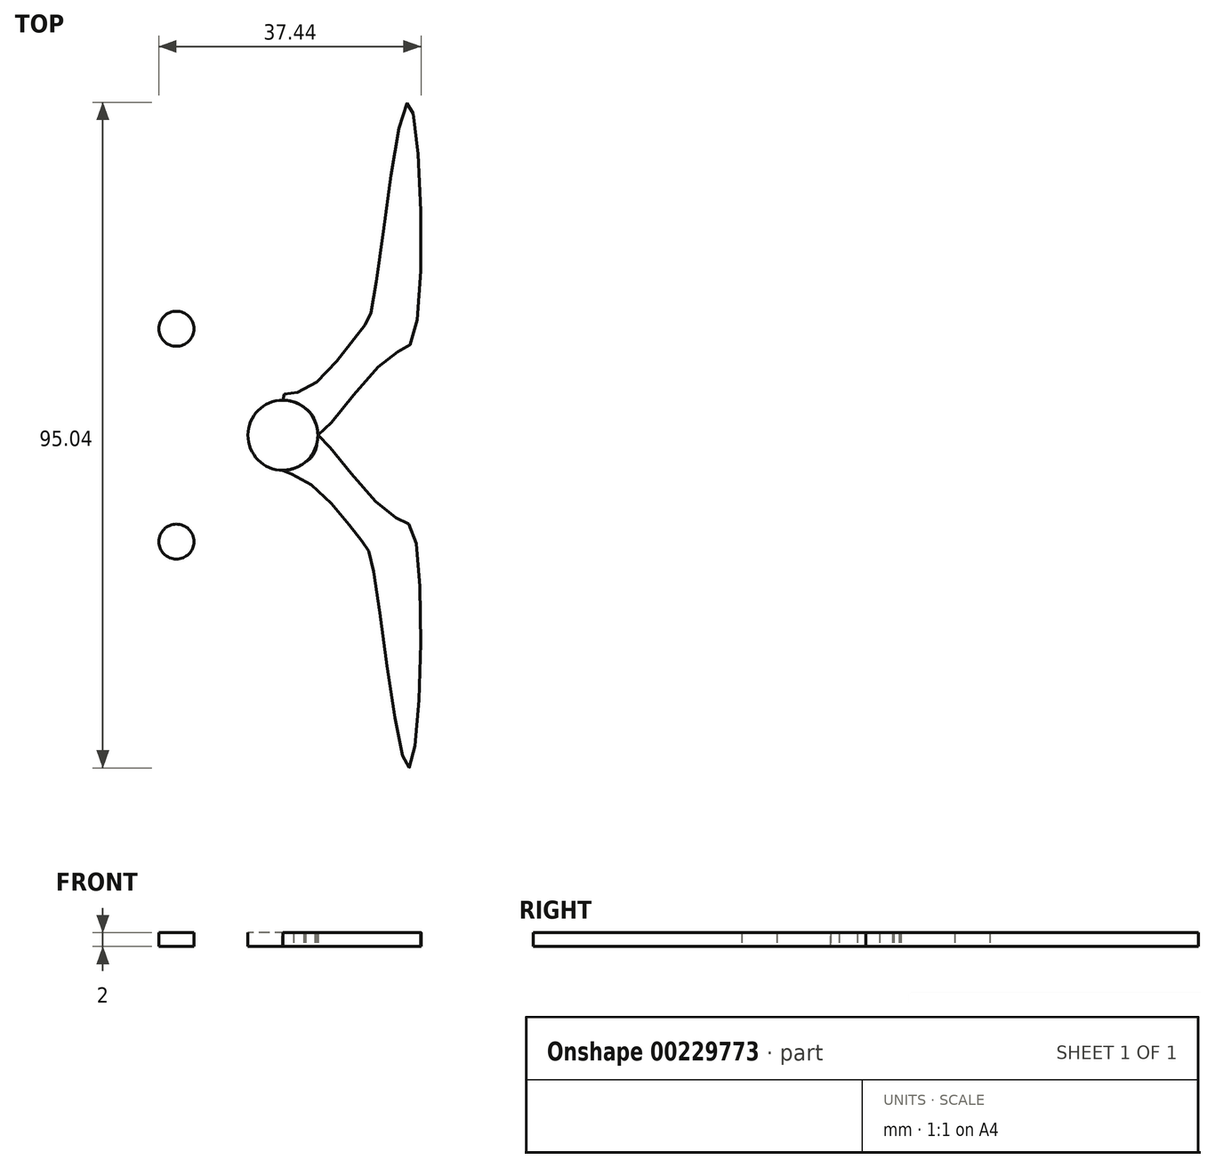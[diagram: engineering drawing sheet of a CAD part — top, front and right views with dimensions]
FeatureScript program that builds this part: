
annotation { "Feature Type Name" : "Feature", "Feature Type Description" : "" }
export const myFeature = defineFeature(function(context is Context, id is Id, definition is map)
    precondition{}
    {
        {
            var Q0;
            Q0=qCreatedBy(makeId("Top.planeOp"),FACE);
            var sketch = newSketch(context, id + "F0", { "sketchPlane" : qUnion([Q0])});
            skCircle(sketch, "E0", {"center": v(0, 0) * mm, "radius": 5 * mm});
            skCircle(sketch, "E1", {"center": v(-15.2, 15.2) * mm, "radius": 2.5 * mm});
            skFitSpline(sketch, "E2", {"points": [v(-5, 0) * mm, v(-15.31, 11.3) * mm, v(-18.74, 14.12) * mm, v(-17.97, 47.52) * mm, v(-12.83, 18.58) * mm, v(-11.2, 15.06) * mm, v(-3.24, 6.5) * mm, v(0, 5.73) * mm, v(0, 5) * mm, v(-5, 0) * mm, v(-5, 0) * mm, v(-5, 0) * mm]});
            skFitSpline(sketch, "E3.MirrorC", {"points": [v(5, 0) * mm, v(15.31, 11.3) * mm, v(18.74, 14.12) * mm, v(17.97, 47.52) * mm, v(12.83, 18.58) * mm, v(11.2, 15.06) * mm, v(3.24, 6.5) * mm, v(0, 5.73) * mm, v(0, 5) * mm, v(5, 0) * mm, v(5, 0) * mm, v(5, 0) * mm]});
            skCircle(sketch, "E4.MirrorC", {"center": v(15.2, 15.2) * mm, "radius": 2.5 * mm});
            skCircle(sketch, "E5.MirrorC", {"center": v(-15.2, -15.2) * mm, "radius": 2.5 * mm});
            skCircle(sketch, "E6.MirrorC", {"center": v(15.2, -15.2) * mm, "radius": 2.5 * mm});
            skFitSpline(sketch, "E7", {"points": [v(0, 5.73) * mm, v(-3.24, 6.5) * mm, v(-11.2, 15.06) * mm, v(-11.2, 16.1) * mm, v(-12.83, 18.58) * mm, v(-17.97, 47.52) * mm, v(-18.74, 14.12) * mm, v(-15.31, 11.3) * mm, v(-5, 0) * mm, v(0, 5) * mm, v(0, 5) * mm, v(0, 5) * mm, v(0, 5) * mm, v(0, 5.73) * mm]});
            skFitSpline(sketch, "E8", {"points": [v(0, 5) * mm, v(0, 5.73) * mm, v(3.24, 6.5) * mm, v(11.2, 15.06) * mm, v(12.83, 18.58) * mm, v(17.97, 47.52) * mm, v(18.74, 14.12) * mm, v(15.31, 11.3) * mm, v(5, 0) * mm, v(0, 5) * mm, v(0, 5) * mm, v(0, 5) * mm]});
            skFitSpline(sketch, "E9.MirrorC", {"points": [v(0, -5) * mm, v(0, -5.73) * mm, v(3.24, -6.5) * mm, v(11.2, -15.06) * mm, v(12.83, -18.58) * mm, v(17.97, -47.52) * mm, v(18.74, -14.12) * mm, v(15.31, -11.3) * mm, v(5, 0) * mm, v(0, -5) * mm, v(0, -5) * mm, v(0, -5) * mm]});
            skFitSpline(sketch, "E10.MirrorC", {"points": [v(0, -5.73) * mm, v(-3.24, -6.5) * mm, v(-11.2, -15.06) * mm, v(-11.2, -16.1) * mm, v(-12.83, -18.58) * mm, v(-17.97, -47.52) * mm, v(-18.74, -14.12) * mm, v(-15.31, -11.3) * mm, v(-5, 0) * mm, v(0, -5) * mm, v(0, -5) * mm, v(0, -5) * mm, v(0, -5) * mm, v(0, -5.73) * mm]});
            skFitSpline(sketch, "E11", {"points": [v(0, -5) * mm, v(3.24, -6.5) * mm, v(11.2, -15.06) * mm, v(12.83, -18.58) * mm, v(17.97, -47.52) * mm, v(18.74, -14.12) * mm, v(15.31, -11.3) * mm, v(5, 0) * mm, v(4.86, -1.18) * mm, v(3.24, -3.81) * mm, v(0, -5) * mm]});
            skFitSpline(sketch, "E12", {"points": [v(0, 5) * mm, v(0, 5.73) * mm, v(3.24, 6.5) * mm, v(11.2, 15.06) * mm, v(12.83, 18.58) * mm, v(17.97, 47.52) * mm, v(18.74, 14.12) * mm, v(15.31, 11.3) * mm, v(5, 0) * mm, v(4.59, 1.98) * mm, v(3.24, 3.81) * mm, v(1.55, 4.75) * mm, v(0, 5) * mm]});
            skFitSpline(sketch, "E13", {"points": [v(0, -5) * mm, v(-1.18, -6.06) * mm, v(-0.17, -4.7) * mm, v(0, -5) * mm]});
            skSolve(sketch);
        }
        {
            var Q0;
            Q0=makeQuery(id+"F0.imprint","IMPRINT",FACE,{"disambiguationData":[TD([[makeQuery(id+"F0.imprint","IMPRINT",EDGE,{"derivedFrom":sQuery(id+"F0.wireOp",EDGE,"E1")}),-1.0]])]});
            var Q1;
            Q1=makeQuery(id+"F0.imprint","IMPRINT",FACE,{"disambiguationData":[TD([[makeQuery(id+"F0.imprint","IMPRINT",EDGE,{"derivedFrom":sQuery(id+"F0.wireOp",EDGE,"E4.MirrorC")}),1.0]])]});
            var Q2;
            Q2=makeQuery(id+"F0.imprint","IMPRINT",FACE,{"disambiguationData":[TD([[makeQuery(id+"F0.imprint","IMPRINT",EDGE,{"derivedFrom":sQuery(id+"F0.wireOp",EDGE,"E6.MirrorC")}),-1.0]])]});
            var Q3;
            Q3=makeQuery(id+"F0.imprint","IMPRINT",FACE,{"disambiguationData":[TD([[makeQuery(id+"F0.imprint","IMPRINT",EDGE,{"derivedFrom":sQuery(id+"F0.wireOp",EDGE,"E5.MirrorC")}),1.0]])]});
            var Q4;
            {var subQ0=sQuery(id+"F0.wireOp",EDGE,"E13");var subQ1=sQuery(id+"F0.wireOp",EDGE,"E10.MirrorC");var subQ5=makeQuery(id+"F0.imprint","INTERSECT",VERTEX,{"disambiguationData":[OD(0.0)],"derivedFrom":[subQ1,subQ0]});Q4=makeQuery(id+"F0.imprint","IMPRINT",FACE,{"disambiguationData":[TD([[makeQuery(id+"F0.imprint","IMPRINT",EDGE,{"disambiguationData":[TD([[subQ5,1.0]])],"derivedFrom":subQ1}),-1.0]])]});}
            var Q5;
            {var subQ0=sQuery(id+"F0.wireOp",EDGE,"E12");var subQ1=sQuery(id+"F0.wireOp",EDGE,"E7");var subQ2=makeQuery(id+"F0.imprint","INTERSECT",VERTEX,{"derivedFrom":[subQ1,subQ0]});Q5=makeQuery(id+"F0.imprint","IMPRINT",FACE,{"disambiguationData":[TD([[makeQuery(id+"F0.imprint","IMPRINT",EDGE,{"disambiguationData":[TD([[subQ2,1.0]])],"derivedFrom":subQ1}),1.0]])]});}
            var Q6;
            Q6=makeQuery(id+"F0.imprint","IMPRINT",FACE,{"disambiguationData":[TD([[makeQuery(id+"F0.imprint","IMPRINT",EDGE,{"derivedFrom":sQuery(id+"F0.wireOp",EDGE,"E1")}),1.0]])]});
            var Q7;
            Q7=makeQuery(id+"F0.imprint","IMPRINT",FACE,{"disambiguationData":[TD([[makeQuery(id+"F0.imprint","IMPRINT",EDGE,{"derivedFrom":sQuery(id+"F0.wireOp",EDGE,"E4.MirrorC")}),-1.0]])]});
            var Q8;
            Q8=makeQuery(id+"F0.imprint","IMPRINT",FACE,{"disambiguationData":[TD([[makeQuery(id+"F0.imprint","IMPRINT",EDGE,{"derivedFrom":sQuery(id+"F0.wireOp",EDGE,"E5.MirrorC")}),-1.0]])]});
            var Q9;
            Q9=makeQuery(id+"F0.imprint","IMPRINT",FACE,{"disambiguationData":[TD([[makeQuery(id+"F0.imprint","IMPRINT",EDGE,{"derivedFrom":sQuery(id+"F0.wireOp",EDGE,"E6.MirrorC")}),1.0]])]});
            extrude(context, id + "F1", {"entities" : qUnion([Q0, Q1, Q2, Q3, Q4, Q5, Q6, Q7, Q8, Q9]), "depth" : 2 * mm, "offsetDistance" : 25.4 * mm});
        }
        {
            var Q0;
            Q0=qCreatedBy(makeId("Top.planeOp"),FACE);
            var sketch = newSketch(context, id + "F2", { "sketchPlane" : qUnion([Q0])});
            skCircle(sketch, "E14", {"center": v(0, 0) * mm, "radius": 5 * mm});
            skSolve(sketch);
        }
        {
            var Q0;
            Q0=makeQuery(id+"F2.imprint","IMPRINT",FACE,{"disambiguationData":[TD([[makeQuery(id+"F2.imprint","IMPRINT",EDGE,{"derivedFrom":sQuery(id+"F2.wireOp",EDGE,"E14")}),1.0]])]});
            extrude(context, id + "F3", {"entities" : qUnion([Q0]), "depth" : 2 * mm, "offsetDistance" : 25.4 * mm});
        }
    });
